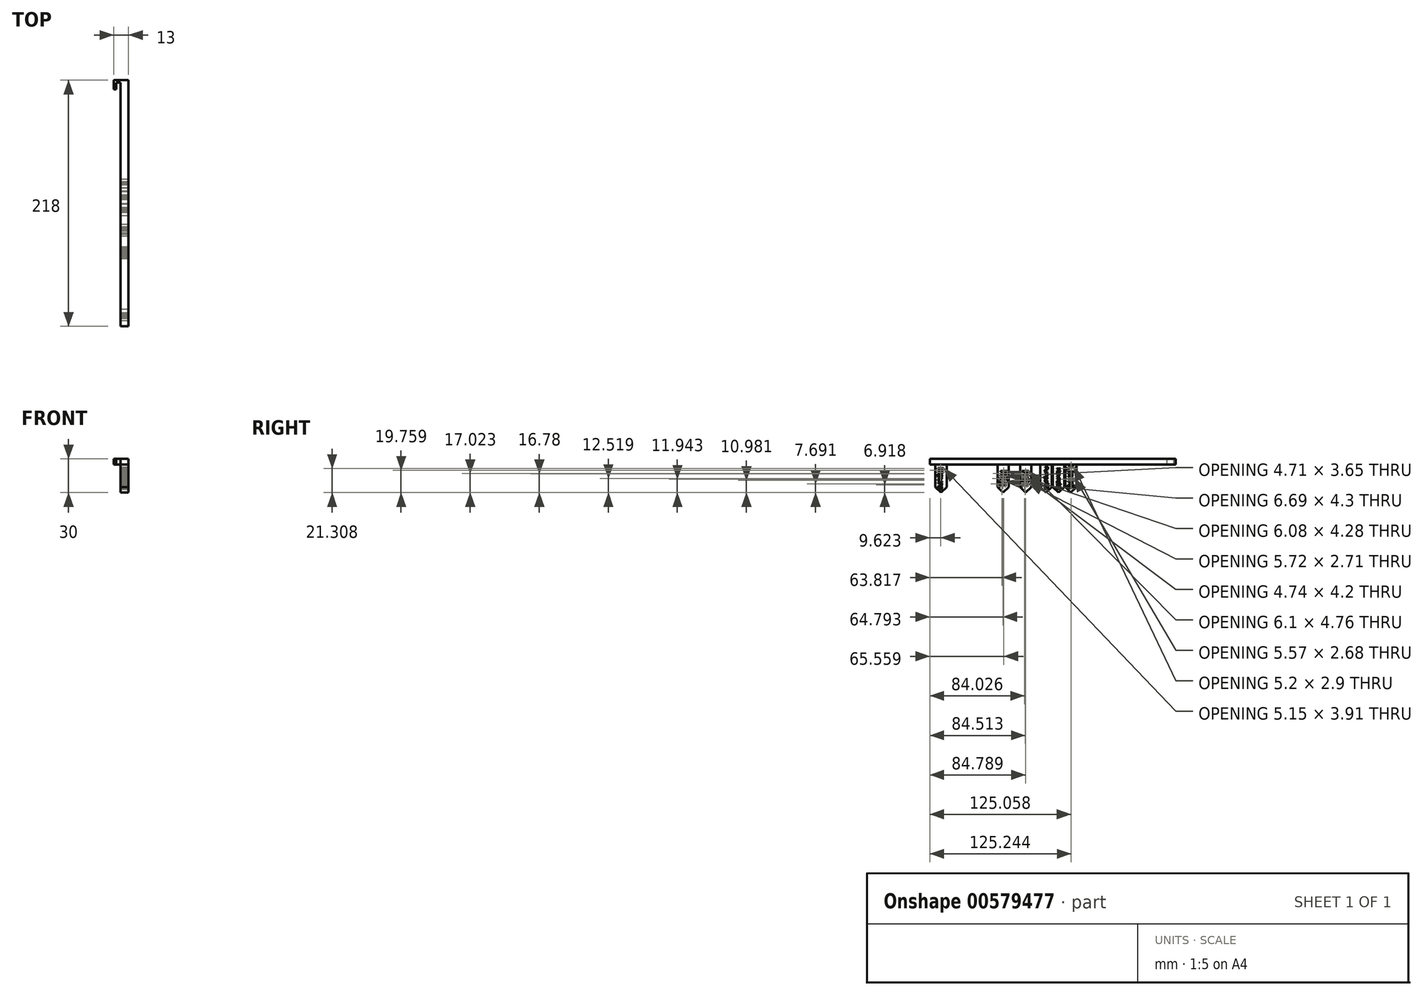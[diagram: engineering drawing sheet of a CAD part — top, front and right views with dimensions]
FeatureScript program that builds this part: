
annotation { "Feature Type Name" : "Feature", "Feature Type Description" : "" }
export const myFeature = defineFeature(function(context is Context, id is Id, definition is map)
    precondition{}
    {
        {
            var Q0;
            Q0=qCreatedBy(makeId("Top.planeOp"),FACE);
            var sketch = newSketch(context, id + "F0", { "sketchPlane" : qUnion([Q0])});
            skLineSegment(sketch, "E0", {"start": v(0, 0) * mm, "end": v(0, 218) * mm});
            skLineSegment(sketch, "E1", {"start": v(0, 218) * mm, "end": v(-13, 218) * mm});
            skLineSegment(sketch, "E2", {"start": v(-13, 218) * mm, "end": v(-13, 210) * mm});
            skLineSegment(sketch, "E3", {"start": v(-13, 210) * mm, "end": v(-11, 210) * mm});
            skLineSegment(sketch, "E4", {"start": v(-11, 210) * mm, "end": v(-11, 216) * mm});
            skLineSegment(sketch, "E5", {"start": v(-11, 216) * mm, "end": v(-7, 216) * mm});
            skLineSegment(sketch, "E6", {"start": v(-7, 216) * mm, "end": v(-7, 0) * mm});
            skLineSegment(sketch, "E7", {"start": v(-7, 0) * mm, "end": v(0, 0) * mm});
            skSolve(sketch);
        }
        {
            var Q0;
            Q0=makeQuery(id+"F0.imprint","IMPRINT",FACE,{"disambiguationData":[TD([[makeQuery(id+"F0.imprint","IMPRINT",EDGE,{"derivedFrom":sQuery(id+"F0.wireOp",EDGE,"E0")}),1.0]])]});
            extrude(context, id + "F1", {"entities" : qUnion([Q0]), "depth" : 5 * mm, "offsetDistance" : 25 * mm});
        }
        {
            var Q0;
            Q0=makeQuery(id+"F1.opExtrude","CAP_FACE",FACE,{"disambiguationData":[OSD([sQuery(id+"F0.wireOp",EDGE,"E0"),sQuery(id+"F0.wireOp",EDGE,"E1"),sQuery(id+"F0.wireOp",EDGE,"E2"),sQuery(id+"F0.wireOp",EDGE,"E3"),sQuery(id+"F0.wireOp",EDGE,"E4"),sQuery(id+"F0.wireOp",EDGE,"E5"),sQuery(id+"F0.wireOp",EDGE,"E6"),sQuery(id+"F0.wireOp",EDGE,"E7")])],"isStart":true});
            var sketch = newSketch(context, id + "F2", { "sketchPlane" : qUnion([Q0])});
            skLineSegment(sketch, "E8.bottom", {"start": v(0, -5) * mm, "end": v(-7, -5) * mm});
            skLineSegment(sketch, "E8.top", {"start": v(0, -15) * mm, "end": v(-7, -15) * mm});
            skLineSegment(sketch, "E8.left", {"start": v(0, -5) * mm, "end": v(0, -15) * mm});
            skLineSegment(sketch, "E8.right", {"start": v(-7, -5) * mm, "end": v(-7, -15) * mm});
            skLineSegment(sketch, "E9.bottom", {"start": v(-7, -60) * mm, "end": v(0, -60) * mm});
            skLineSegment(sketch, "E9.top", {"start": v(-7, -70) * mm, "end": v(0, -70) * mm});
            skLineSegment(sketch, "E9.left", {"start": v(-7, -60) * mm, "end": v(-7, -70) * mm});
            skLineSegment(sketch, "E9.right", {"start": v(0, -60) * mm, "end": v(0, -70) * mm});
            skLineSegment(sketch, "E10.bottom", {"start": v(0, -80) * mm, "end": v(-7, -80) * mm});
            skLineSegment(sketch, "E10.top", {"start": v(0, -90) * mm, "end": v(-7, -90) * mm});
            skLineSegment(sketch, "E10.left", {"start": v(0, -80) * mm, "end": v(0, -90) * mm});
            skLineSegment(sketch, "E10.right", {"start": v(-7, -80) * mm, "end": v(-7, -90) * mm});
            skLineSegment(sketch, "E11.bottom", {"start": v(0, -109) * mm, "end": v(-7, -109) * mm});
            skLineSegment(sketch, "E11.top", {"start": v(0, -119) * mm, "end": v(-7, -119) * mm});
            skLineSegment(sketch, "E11.left", {"start": v(0, -109) * mm, "end": v(0, -119) * mm});
            skLineSegment(sketch, "E11.right", {"start": v(-7, -109) * mm, "end": v(-7, -119) * mm});
            skLineSegment(sketch, "E12.bottom", {"start": v(-7, -98) * mm, "end": v(0, -98) * mm});
            skLineSegment(sketch, "E12.top", {"start": v(-7, -108) * mm, "end": v(0, -108) * mm});
            skLineSegment(sketch, "E12.left", {"start": v(-7, -98) * mm, "end": v(-7, -108) * mm});
            skLineSegment(sketch, "E12.right", {"start": v(0, -98) * mm, "end": v(0, -108) * mm});
            skLineSegment(sketch, "E13.bottom", {"start": v(-7, -120) * mm, "end": v(0, -120) * mm});
            skLineSegment(sketch, "E13.top", {"start": v(-7, -130) * mm, "end": v(0, -130) * mm});
            skLineSegment(sketch, "E13.left", {"start": v(-7, -120) * mm, "end": v(-7, -130) * mm});
            skLineSegment(sketch, "E13.right", {"start": v(0, -120) * mm, "end": v(0, -130) * mm});
            skSolve(sketch);
        }
        {
            var Q0;
            Q0 = qSketchRegion(id + "F2", true);
            extrude(context, id + "F3", {"entities" : qUnion([Q0]), "depth" : 25 * mm, "offsetDistance" : 25 * mm});
        }
        {
            var Q0;
            Q0=makeQuery(id+"F3.opExtrude","SWEPT_FACE",FACE,{"disambiguationData":[OSD([sQuery(id+"F2.wireOp",EDGE,"E13.right")])]});
            var sketch = newSketch(context, id + "F4", { "sketchPlane" : qUnion([Q0])});
            skText(sketch, "E14", { "text": "Linfrö\n", "fontName": "OpenSans-Regular.ttf"});
            const initialGuessF4  = {"E14": [0.12246, -0.00153, 0, -1, 0.00524]};
            skSetInitialGuess(sketch, initialGuessF4);
            skSolve(sketch);
        }
        {
            var Q0;
            Q0 = qSketchRegion(id + "F4", true);
            extrude(context, id + "F5", {"entities" : qUnion([Q0]), "operationType" : NewBodyOperationType.REMOVE, "endBound" : BoundingType.UP_TO_NEXT, "oppositeDirection" : true, "depth" : 25 * mm, "offsetDistance" : 25 * mm});
        }
        {
            var Q0;
            Q0=makeQuery(id+"F3.opExtrude","SWEPT_FACE",FACE,{"disambiguationData":[OSD([sQuery(id+"F2.wireOp",EDGE,"E11.left")])]});
            var sketch = newSketch(context, id + "F6", { "sketchPlane" : qUnion([Q0])});
            skText(sketch, "E15", { "text": "Havrekli\n", "fontName": "OpenSans-Regular.ttf"});
            skPoint(sketch, "E16", {"position": v(109, -12.5) * mm});
            const initialGuessF6  = {"E15": [0.11243, -0.003, 0, -1, 0.00362]};
            skSetInitialGuess(sketch, initialGuessF6);
            skSolve(sketch);
        }
        {
            var Q0;
            Q0 = qSketchRegion(id + "F6", true);
            extrude(context, id + "F7", {"entities" : qUnion([Q0]), "operationType" : NewBodyOperationType.REMOVE, "endBound" : BoundingType.UP_TO_NEXT, "oppositeDirection" : true, "depth" : 25 * mm, "offsetDistance" : 25 * mm});
        }
        {
            var Q0;
            Q0=makeQuery(id+"F3.opExtrude","SWEPT_FACE",FACE,{"disambiguationData":[OSD([sQuery(id+"F2.wireOp",EDGE,"E12.right")])]});
            var sketch = newSketch(context, id + "F8", { "sketchPlane" : qUnion([Q0])});
            skText(sketch, "E17", { "text": "Pumpafrö", "fontName": "OpenSans-Regular.ttf"});
            const initialGuessF8  = {"E17": [0.10186, -0.0018, 0, -1, 0.00308]};
            skSetInitialGuess(sketch, initialGuessF8);
            skSolve(sketch);
        }
        {
            var Q0;
            Q0 = qSketchRegion(id + "F8", true);
            extrude(context, id + "F9", {"entities" : qUnion([Q0]), "operationType" : NewBodyOperationType.REMOVE, "endBound" : BoundingType.UP_TO_NEXT, "oppositeDirection" : true, "depth" : 25 * mm, "offsetDistance" : 25 * mm});
        }
        {
            var Q0;
            Q0=makeQuery(id+"F3.opExtrude","SWEPT_FACE",FACE,{"disambiguationData":[OSD([sQuery(id+"F2.wireOp",EDGE,"E10.left")])]});
            var sketch = newSketch(context, id + "F10", { "sketchPlane" : qUnion([Q0])});
            skText(sketch, "E18", { "text": "Nöt", "fontName": "OpenSans-Regular.ttf"});
            skPoint(sketch, "E19", {"position": v(90, -12.5) * mm});
            const initialGuessF10  = {"E18": [0.08152, -0.005, 0, -1, 0.00615]};
            skSetInitialGuess(sketch, initialGuessF10);
            skSolve(sketch);
        }
        {
            var Q0;
            Q0 = qSketchRegion(id + "F10", true);
            extrude(context, id + "F11", {"entities" : qUnion([Q0]), "operationType" : NewBodyOperationType.ADD, "endBound" : BoundingType.UP_TO_NEXT, "oppositeDirection" : true, "depth" : 25 * mm, "offsetDistance" : 25 * mm});
        }
        {
            var Q0;
            Q0=makeQuery(id+"F3.opExtrude","SWEPT_FACE",FACE,{"disambiguationData":[OSD([sQuery(id+"F2.wireOp",EDGE,"E10.left")])]});
            var sketch = newSketch(context, id + "F12", { "sketchPlane" : qUnion([Q0])});
            skText(sketch, "E20", { "text": "Nöt", "fontName": "OpenSans-Regular.ttf"});
            skPoint(sketch, "E21", {"position": v(90, -12.5) * mm});
            const initialGuessF12  = {"E20": [0.08174, -0.005, 0, -1, 0.00615]};
            skSetInitialGuess(sketch, initialGuessF12);
            skSolve(sketch);
        }
        {
            var Q0;
            Q0=makeQuery(id+"F3.opExtrude","SWEPT_FACE",FACE,{"disambiguationData":[OSD([sQuery(id+"F2.wireOp",EDGE,"E9.right")])]});
            var sketch = newSketch(context, id + "F13", { "sketchPlane" : qUnion([Q0])});
            skText(sketch, "E22", { "text": "Råg", "fontName": "OpenSans-Regular.ttf"});
            skPoint(sketch, "E23", {"position": v(70, -12.5) * mm});
            const initialGuessF13  = {"E22": [0.06252, -0.005, 0, -1, 0.00613]};
            skSetInitialGuess(sketch, initialGuessF13);
            skSolve(sketch);
        }
        {
            var Q0;
            Q0=makeQuery(id+"F3.opExtrude","SWEPT_FACE",FACE,{"disambiguationData":[OSD([sQuery(id+"F2.wireOp",EDGE,"E8.left")])]});
            var sketch = newSketch(context, id + "F14", { "sketchPlane" : qUnion([Q0])});
            skText(sketch, "E24", { "text": "Havre", "fontName": "OpenSans-Regular.ttf"});
            skPoint(sketch, "E25", {"position": v(15, -12.5) * mm});
            const initialGuessF14  = {"E24": [0.00705, -0.00258, 0, -1, 0.00519]};
            skSetInitialGuess(sketch, initialGuessF14);
            skSolve(sketch);
        }
        {
            var Q0;
            Q0 = qSketchRegion(id + "F12", true);
            extrude(context, id + "F15", {"entities" : qUnion([Q0]), "operationType" : NewBodyOperationType.REMOVE, "oppositeDirection" : true, "depth" : 25 * mm, "offsetDistance" : 25 * mm});
        }
        {
            var Q0;
            Q0 = qSketchRegion(id + "F13", true);
            extrude(context, id + "F16", {"entities" : qUnion([Q0]), "operationType" : NewBodyOperationType.REMOVE, "oppositeDirection" : true, "depth" : 25 * mm, "offsetDistance" : 25 * mm});
        }
        {
            var Q0;
            Q0 = qSketchRegion(id + "F14", true);
            extrude(context, id + "F17", {"entities" : qUnion([Q0]), "operationType" : NewBodyOperationType.REMOVE, "oppositeDirection" : true, "depth" : 25 * mm, "offsetDistance" : 25 * mm});
        }
        {
            var Q0;
            Q0=makeQuery(id+"F3.opExtrude","CAP_EDGE",EDGE,{"disambiguationData":[OSD([sQuery(id+"F2.wireOp",EDGE,"E13.top")])],"isStart":false});
            var Q1;
            Q1=makeQuery(id+"F3.opExtrude","CAP_EDGE",EDGE,{"disambiguationData":[OSD([sQuery(id+"F2.wireOp",EDGE,"E13.bottom")])],"isStart":false});
            var Q2;
            Q2=makeQuery(id+"F3.opExtrude","CAP_EDGE",EDGE,{"disambiguationData":[OSD([sQuery(id+"F2.wireOp",EDGE,"E11.top")])],"isStart":false});
            var Q3;
            Q3=makeQuery(id+"F3.opExtrude","CAP_EDGE",EDGE,{"disambiguationData":[OSD([sQuery(id+"F2.wireOp",EDGE,"E11.bottom")])],"isStart":false});
            var Q4;
            Q4=makeQuery(id+"F3.opExtrude","CAP_EDGE",EDGE,{"disambiguationData":[OSD([sQuery(id+"F2.wireOp",EDGE,"E12.top")])],"isStart":false});
            var Q5;
            Q5=makeQuery(id+"F3.opExtrude","CAP_EDGE",EDGE,{"disambiguationData":[OSD([sQuery(id+"F2.wireOp",EDGE,"E12.bottom")])],"isStart":false});
            var Q6;
            Q6=makeQuery(id+"F3.opExtrude","CAP_EDGE",EDGE,{"disambiguationData":[OSD([sQuery(id+"F2.wireOp",EDGE,"E10.bottom")])],"isStart":false});
            var Q7;
            Q7=makeQuery(id+"F3.opExtrude","CAP_EDGE",EDGE,{"disambiguationData":[OSD([sQuery(id+"F2.wireOp",EDGE,"E10.top")])],"isStart":false});
            var Q8;
            Q8=makeQuery(id+"F3.opExtrude","CAP_EDGE",EDGE,{"disambiguationData":[OSD([sQuery(id+"F2.wireOp",EDGE,"E9.top")])],"isStart":false});
            var Q9;
            Q9=makeQuery(id+"F3.opExtrude","CAP_EDGE",EDGE,{"disambiguationData":[OSD([sQuery(id+"F2.wireOp",EDGE,"E9.bottom")])],"isStart":false});
            var Q10;
            Q10=makeQuery(id+"F3.opExtrude","CAP_EDGE",EDGE,{"disambiguationData":[OSD([sQuery(id+"F2.wireOp",EDGE,"E8.top")])],"isStart":false});
            var Q11;
            Q11=makeQuery(id+"F3.opExtrude","CAP_EDGE",EDGE,{"disambiguationData":[OSD([sQuery(id+"F2.wireOp",EDGE,"E8.bottom")])],"isStart":false});
            chamfer(context, id + "F18", {"entities" : qUnion([Q0, Q1, Q2, Q3, Q4, Q5, Q6, Q7, Q8, Q9, Q10, Q11]), "width" : 5 * mm, "tangentPropagation" : true});
        }
    });
